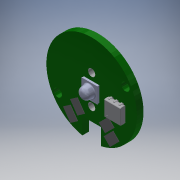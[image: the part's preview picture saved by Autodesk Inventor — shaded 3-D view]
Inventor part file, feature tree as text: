
AUTODESK INVENTOR PART (.ipt)
format: ipt  version: 2018 (Build 220112000, 112)  size: 530,432 bytes
history: native  units: in
note: dims shown in document units (in); Inventor stores cm internally (conversion verified against a paired STEP export)
features: other x15, reference x4, extrude x1, sketch x1
ambient origin geometry x8: Origin, YZ Plane, XZ Plane, XY Plane, X Axis, Y Axis, Z Axis, Center Point
bodies: Solid1 (feature_tree), Solid2 (feature_tree), Solid3 (feature_tree), Solid4 (feature_tree), Solid5 (feature_tree), Solid6 (feature_tree), Solid7 (feature_tree), Solid8 (feature_tree), Solid9 (feature_tree), Solid10 (feature_tree), Solid11 (feature_tree), Solid12 (feature_tree), Solid13 (feature_tree)
feature tree (21):
  other  "944700-1-solid1"
  extrude  "Extrusion2"  Depth=0.0039in
  sketch  "Sketch6"  dims[d7=0.0039in d8=0.0039in d9=0.0787in d10=0.0in]
  reference  "Reference1"
  reference  "Reference2"
  reference  "Reference3"
  reference  "Reference4"
  other  "944700-1-solid2"
  other  "944700-1-solid3"
  other  "944700-1-solid4"
  other  "944700-1-solid5"
  other  "944700-1-solid6"
  other  "944700-1-solid7"
  other  "944700-1-solid8"
  other  "944700-1-solid9"
  other  "944700-1-solid10"
  other  "944700-1-solid11"
  other  "944700-1-solid12"
  other  "Osram Oslon Black-1-solid1"
  other  "Assembly1"
  other  "front:1"
